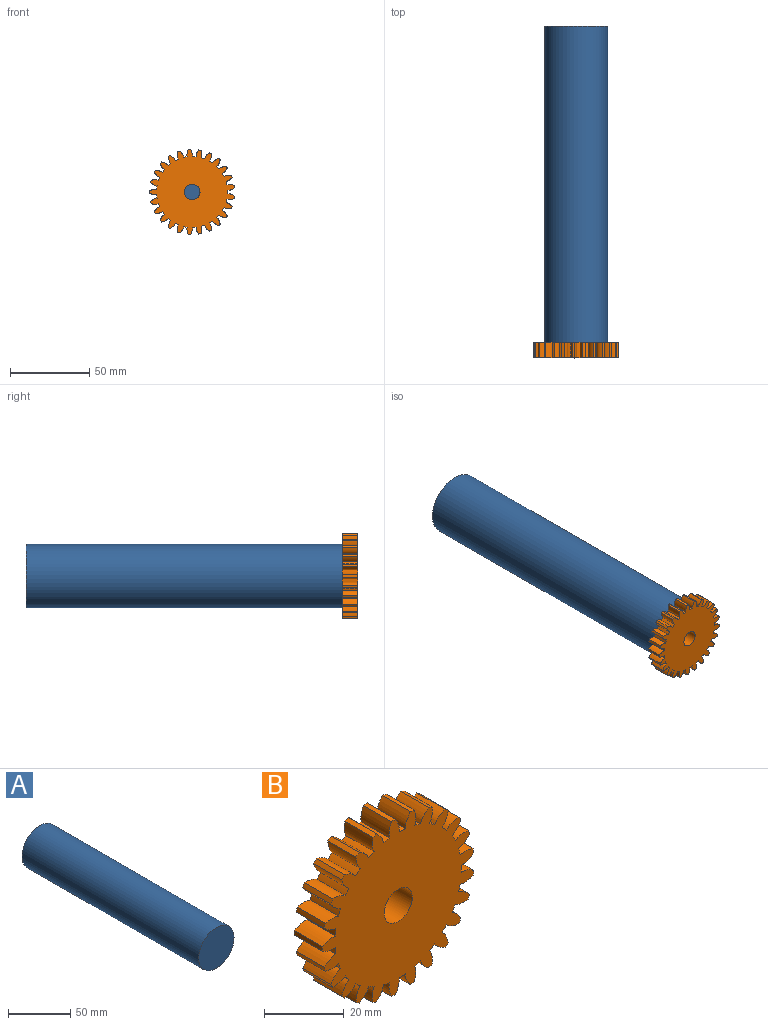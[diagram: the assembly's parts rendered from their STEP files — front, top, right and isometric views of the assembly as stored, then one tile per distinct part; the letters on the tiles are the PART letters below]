
ASSEMBLY  parts=2 mates=1
PART A: 3 faces, bbox 40x200x40 mm
  f0: cylinder r=20mm len=200mm, axis (0,-1,0), area 25132.7mm2, adj f1,f2
  f1: plane 40x40mm, normal (0,-1,0), area 1256.6mm2, adj f0
  f2: plane 40x40mm, normal (0,1,0), area 1256.6mm2, adj f0
PART B: 103 faces, bbox 53.9x10x54 mm
  f0: cylinder r=27mm len=10mm, axis (0,1,0), area 14.4mm2, adj f25,f26,f78,f101
  f1: cylinder r=27mm len=10mm, axis (0,1,0), area 14.4mm2, adj f25,f26,f98,f99
  f2: cylinder r=27mm len=10mm, axis (0,1,0), area 14.4mm2, adj f25,f26,f90,f95
  f3: cylinder r=27mm len=10mm, axis (0,1,0), area 14.4mm2, adj f25,f26,f92,f96
  f4: cylinder r=27mm len=10mm, axis (0,1,0), area 14.4mm2, adj f25,f26,f84,f89
  f5: cylinder r=27mm len=10mm, axis (0,1,0), area 14.4mm2, adj f25,f26,f75,f86
  f6: cylinder r=27mm len=10mm, axis (0,1,0), area 14.4mm2, adj f25,f26,f83,f87
  f7: cylinder r=27mm len=10mm, axis (0,1,0), area 14.4mm2, adj f25,f26,f80,f81
  f8: cylinder r=27mm len=10mm, axis (0,1,0), area 14.4mm2, adj f25,f26,f72,f77
  f9: cylinder r=27mm len=10mm, axis (0,1,0), area 14.4mm2, adj f25,f26,f69,f74
  f10: cylinder r=27mm len=10mm, axis (0,1,0), area 14.4mm2, adj f25,f26,f66,f71
  f11: cylinder r=27mm len=10mm, axis (0,1,0), area 14.4mm2, adj f25,f26,f57,f68
  f12: cylinder r=27mm len=10mm, axis (0,1,0), area 14.4mm2, adj f25,f26,f27,f65
  f13: cylinder r=27mm len=10mm, axis (0,1,0), area 14.4mm2, adj f25,f26,f62,f63
  f14: cylinder r=27mm len=10mm, axis (0,1,0), area 14.4mm2, adj f25,f26,f54,f59
  f15: cylinder r=27mm len=10mm, axis (0,1,0), area 14.4mm2, adj f25,f26,f56,f60
  f16: cylinder r=27mm len=10mm, axis (0,1,0), area 14.4mm2, adj f25,f26,f53,f93
  f17: cylinder r=27mm len=10mm, axis (0,1,0), area 14.4mm2, adj f25,f26,f50,f51
  f18: cylinder r=27mm len=10mm, axis (0,1,0), area 14.4mm2, adj f25,f26,f47,f48
  f19: cylinder r=27mm len=10mm, axis (0,1,0), area 14.4mm2, adj f25,f26,f44,f45
  f20: cylinder r=27mm len=10mm, axis (0,1,0), area 14.4mm2, adj f25,f26,f36,f41
  f21: cylinder r=27mm len=10mm, axis (0,1,0), area 14.4mm2, adj f25,f26,f30,f38
  f22: cylinder r=27mm len=10mm, axis (0,1,0), area 14.4mm2, adj f25,f26,f35,f42
  f23: cylinder r=27mm len=10mm, axis (0,1,0), area 14.4mm2, adj f25,f26,f32,f33
  f24: cylinder r=27mm len=10mm, axis (0,1,0), area 14.4mm2, adj f25,f26,f29,f39
  f25: plane 54.03x53.92mm, normal (0,-1,0), area 1850.1mm2, adj f0,f1,f2,f3,f4,f5,f6,f7
  f26: plane 54.03x53.92mm, normal (0,1,0), area 1850.1mm2, adj f0,f1,f2,f3,f4,f5,f6,f7
  f27: extruded ~10x4.39mm, area 47.6mm2, adj f12,f25,f26,f28
  f28: cylinder r=22.5mm len=10mm, axis (0,1,0), area 21.6mm2, adj f25,f26,f27,f29
  f29: extruded ~10x4.39mm, area 47.6mm2, adj f24,f25,f26,f28
  f30: extruded ~10x4.29mm, area 47.6mm2, adj f21,f25,f26,f31
  f31: cylinder r=22.5mm len=10mm, axis (0,1,0), area 21.6mm2, adj f25,f26,f30,f32
  f32: extruded ~10x4.17mm, area 47.6mm2, adj f23,f25,f26,f31
  f33: extruded ~10x3.7mm, area 47.6mm2, adj f23,f25,f26,f34
  f34: cylinder r=22.5mm len=10mm, axis (0,1,0), area 21.6mm2, adj f25,f26,f33,f35
  f35: extruded ~10x4.56mm, area 47.6mm2, adj f22,f25,f26,f34
  f36: extruded ~10x4.62mm, area 47.6mm2, adj f20,f25,f26,f37
  f37: cylinder r=22.5mm len=10mm, axis (0,1,0), area 21.6mm2, adj f25,f26,f36,f38
  f38: extruded ~10x3.51mm, area 47.6mm2, adj f21,f25,f26,f37
  f39: extruded ~10x4.65mm, area 47.6mm2, adj f24,f25,f26,f40
  f40: cylinder r=22.5mm len=10mm, axis (0,1,0), area 21.6mm2, adj f25,f26,f39,f41
  f41: extruded ~10x3.86mm, area 47.6mm2, adj f20,f25,f26,f40
  f42: extruded ~10x3.69mm, area 47.6mm2, adj f22,f25,f26,f43
  f43: cylinder r=22.5mm len=10mm, axis (0,1,0), area 21.6mm2, adj f25,f26,f42,f44
  f44: extruded ~10x4.67mm, area 47.6mm2, adj f19,f25,f26,f43
  f45: extruded ~10x4.29mm, area 47.6mm2, adj f19,f25,f26,f46
  f46: cylinder r=22.5mm len=10mm, axis (0,1,0), area 21.6mm2, adj f25,f26,f45,f47
  f47: extruded ~10x4.48mm, area 47.6mm2, adj f18,f25,f26,f46
  f48: extruded ~10x4.61mm, area 47.6mm2, adj f18,f25,f26,f49
  f49: cylinder r=22.5mm len=10mm, axis (0,1,0), area 21.6mm2, adj f25,f26,f48,f50
  f50: extruded ~10x4.02mm, area 47.6mm2, adj f17,f25,f26,f49
  f51: extruded ~10x4.65mm, area 47.6mm2, adj f17,f25,f26,f52
  f52: cylinder r=22.5mm len=10mm, axis (0,1,0), area 21.6mm2, adj f25,f26,f51,f53
  f53: extruded ~10x3.31mm, area 47.6mm2, adj f16,f25,f26,f52
  f54: extruded ~10x4.17mm, area 47.6mm2, adj f14,f25,f26,f55
  f55: cylinder r=22.5mm len=10mm, axis (0,1,0), area 21.6mm2, adj f25,f26,f54,f56
  f56: extruded ~10x4.29mm, area 47.6mm2, adj f15,f25,f26,f55
  f57: extruded ~10x4.56mm, area 47.6mm2, adj f11,f25,f26,f58
  f58: cylinder r=22.5mm len=10mm, axis (0,1,0), area 21.6mm2, adj f25,f26,f57,f59
  f59: extruded ~10x3.7mm, area 47.6mm2, adj f14,f25,f26,f58
  f60: extruded ~10x3.51mm, area 47.6mm2, adj f15,f25,f26,f61
  f61: cylinder r=22.5mm len=10mm, axis (0,1,0), area 21.6mm2, adj f25,f26,f60,f62
  f62: extruded ~10x4.62mm, area 47.6mm2, adj f13,f25,f26,f61
  f63: extruded ~10x3.86mm, area 47.6mm2, adj f13,f25,f26,f64
  f64: cylinder r=22.5mm len=10mm, axis (0,1,0), area 21.6mm2, adj f25,f26,f63,f65
  f65: extruded ~10x4.65mm, area 47.6mm2, adj f12,f25,f26,f64
  f66: extruded ~10x4.67mm, area 47.6mm2, adj f10,f25,f26,f67
  f67: cylinder r=22.5mm len=10mm, axis (0,1,0), area 21.6mm2, adj f25,f26,f66,f68
  f68: extruded ~10x3.69mm, area 47.6mm2, adj f11,f25,f26,f67
  f69: extruded ~10x4.48mm, area 47.6mm2, adj f9,f25,f26,f70
  f70: cylinder r=22.5mm len=10mm, axis (0,1,0), area 21.6mm2, adj f25,f26,f69,f71
  f71: extruded ~10x4.29mm, area 47.6mm2, adj f10,f25,f26,f70
  f72: extruded ~10x4.02mm, area 47.6mm2, adj f8,f25,f26,f73
  f73: cylinder r=22.5mm len=10mm, axis (0,1,0), area 21.6mm2, adj f25,f26,f72,f74
  f74: extruded ~10x4.61mm, area 47.6mm2, adj f9,f25,f26,f73
  f75: extruded ~10x3.31mm, area 47.6mm2, adj f5,f25,f26,f76
  f76: cylinder r=22.5mm len=10mm, axis (0,1,0), area 21.6mm2, adj f25,f26,f75,f77
  f77: extruded ~10x4.65mm, area 47.6mm2, adj f8,f25,f26,f76
  f78: extruded ~10x4.56mm, area 47.6mm2, adj f0,f25,f26,f79
  f79: cylinder r=22.5mm len=10mm, axis (0,1,0), area 21.6mm2, adj f25,f26,f78,f80
  f80: extruded ~10x4.16mm, area 47.6mm2, adj f7,f25,f26,f79
  f81: extruded ~10x4.67mm, area 47.6mm2, adj f7,f25,f26,f82
  f82: cylinder r=22.5mm len=10mm, axis (0,1,0), area 21.6mm2, adj f25,f26,f81,f83
  f83: extruded ~10x3.5mm, area 47.6mm2, adj f6,f25,f26,f82
  f84: extruded ~10x4.03mm, area 47.6mm2, adj f4,f25,f26,f85
  f85: cylinder r=22.5mm len=10mm, axis (0,1,0), area 21.6mm2, adj f25,f26,f84,f86
  f86: extruded ~10x4.4mm, area 47.6mm2, adj f5,f25,f26,f85
  f87: extruded ~10x4.49mm, area 47.6mm2, adj f6,f25,f26,f88
  f88: cylinder r=22.5mm len=10mm, axis (0,1,0), area 21.6mm2, adj f25,f26,f87,f89
  f89: extruded ~10x3.87mm, area 47.6mm2, adj f4,f25,f26,f88
  f90: extruded ~10x3.87mm, area 47.6mm2, adj f2,f25,f26,f91
  f91: cylinder r=22.5mm len=10mm, axis (0,1,0), area 21.6mm2, adj f25,f26,f90,f92
  f92: extruded ~10x4.49mm, area 47.6mm2, adj f3,f25,f26,f91
  f93: extruded ~10x4.4mm, area 47.6mm2, adj f16,f25,f26,f94
  f94: cylinder r=22.5mm len=10mm, axis (0,1,0), area 21.6mm2, adj f25,f26,f93,f95
  f95: extruded ~10x4.03mm, area 47.6mm2, adj f2,f25,f26,f94
  f96: extruded ~10x3.5mm, area 47.6mm2, adj f3,f25,f26,f97
  f97: cylinder r=22.5mm len=10mm, axis (0,1,0), area 21.6mm2, adj f25,f26,f96,f98
  f98: extruded ~10x4.67mm, area 47.6mm2, adj f1,f25,f26,f97
  f99: extruded ~10x4.16mm, area 47.6mm2, adj f1,f25,f26,f100
  f100: cylinder r=22.5mm len=10mm, axis (0,1,0), area 21.6mm2, adj f25,f26,f99,f101
  f101: extruded ~10x4.56mm, area 47.6mm2, adj f0,f25,f26,f100
  f102: cylinder r=5mm len=10mm, axis (0,1,0), area 314.2mm2, adj f25,f26
PLACE A t=(-82.86,119.97,-48.02)mm
PLACE B t=(-82.86,-80.03,-48.02)mm
MATE fastened A.f0 <-> B.f0  axis (0,-1,0) through (-82.86,-80.03,-48.02)mm
